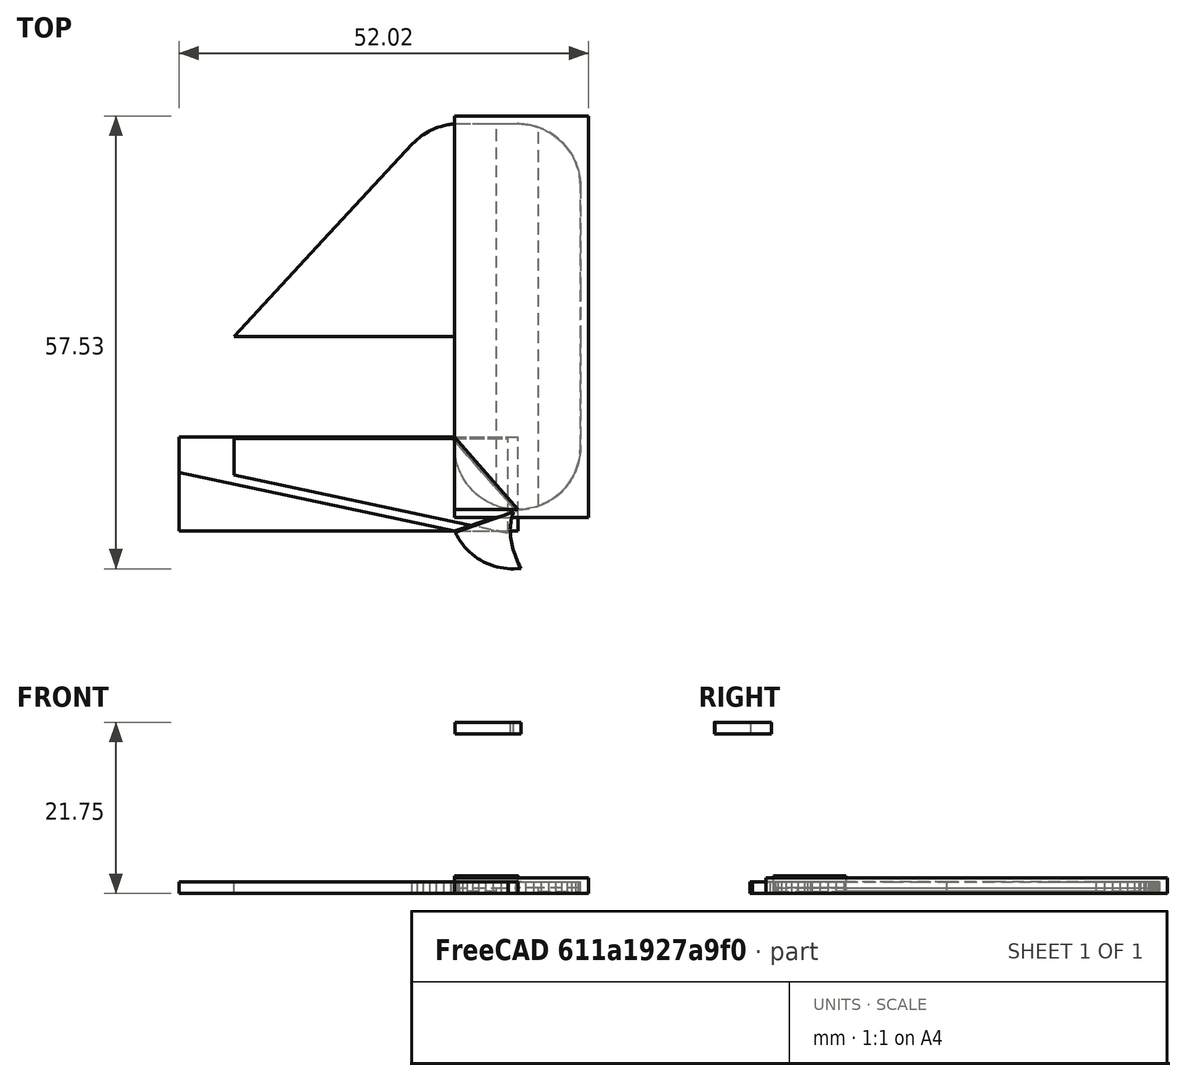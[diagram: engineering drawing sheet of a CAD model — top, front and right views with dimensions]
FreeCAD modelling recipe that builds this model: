
FCSTD DOCUMENT  (FreeCAD 0.18.3R)
Label: Vertical Stabilizer New
License: All rights reserved
LicenseURL: http://en.wikipedia.org/wiki/All_rights_reserved
objects: Part::FeaturePython×24, Part::Feature×8, App::DocumentObjectGroup×6, Part::Extrusion×5, Part::Box×4, Sketcher::SketchObject×4, Mesh::Feature×2, Part::Face×2, Part::Fillet×1
note: 48 computed .brp shape members not serialized (recipe doc carries the construction recipe); baked Part::Feature solids carry a one-line shape summary decoded from their .brp

FEATURE [Mesh::Feature] Vertical_Stabilizer  label="Vertical Stabilizer"
FEATURE [Part::Feature] Vertical_Stabilizer001
  shape: bbox 55.59 x 60.75 x 1.502 mm, 2716 faces, 0 solids (baked)
FEATURE [Part::Feature] Vertical_Stabilizer001_cs
  Placement = pos=(-6.8,0,-0.75) rot=(0,0,1;0rad)
  shape: bbox 44 x 49 x 3e-07 mm, 0 faces, 0 solids (baked)
FEATURE [Mesh::Feature] Fuselage_Full  label="Fuselage Full"
  Placement = pos=(0,0,0) rot=(0,0,1;-1.5708rad)
FEATURE [Part::Face] Face
  FaceMakerClass = Part::FaceMakerBullseye
  Sources = -> [Vertical_Stabilizer001_cs]
FEATURE [Part::Extrusion] Extrude
  Base = -> Face
  Dir = (0,0,1)
  DirMode = 0
  FaceMakerClass = Part::FaceMakerBullseye
  LengthFwd = 1.5
  LengthRev = 0
  Solid = false
  Symmetric = false
FEATURE [Part::Box] Box003  label="Cube003"
  AttacherType = Attacher::AttachEngine3D
  Height = 1.5
  Length = 34.8186
  Placement = pos=(0,-3,0) rot=(0,0,1;0rad)
  Width = 12
FEATURE [Part::Feature] Face004
  Placement = pos=(0,4.3651,0) rot=(0,0,-1;0.208436rad)
  shape: bbox 41.09 x 8.691 x 10 mm, 1 faces, 0 solids (baked)
FEATURE [Part::FeaturePython] Slice003  # WARN: FeaturePython — macro-defined, semantics opaque (R4)
  Base = -> Box003
  Mode = 1
  Tolerance = 0
  Tools = -> [Face004]
FEATURE [Part::FeaturePython] Slice003_child1  label="Slice003.1"  # WARN: FeaturePython — macro-defined, semantics opaque (R4)
  Base = -> Slice003
  FilterType = 1
  Invert = false
  OverrideMaxVal = 0
  WindowFrom = 80
  WindowTo = 100
  items = 1
FEATURE [Part::Feature] Fuselage_Full001
  Placement = pos=(28.0186,13.3054,0) rot=(-1,0,0;1.5708rad)
  shape: bbox 193.7 x 39.83 x 30.14 mm, 4342 faces, 0 solids (baked)
  expr: Placement.Base.y = 13 + 22 - 21.6946
FEATURE [Part::Box] Box  label="Cube"
  AttacherType = Attacher::AttachEngine3D
  Height = 1.5
  Length = 43.0686
  Placement = pos=(-7,-2.6946,0) rot=(0,0,1;0rad)
  Width = 11.9046
FEATURE [Part::Feature] Face005
  Placement = pos=(-7,4.713,0) rot=(0,0,-1;0.208436rad)
  shape: bbox 41.09 x 8.691 x 10 mm, 1 faces, 0 solids (baked)
FEATURE [Sketcher::SketchObject] Sketch
  sketch-geometry (1):
    g0: LineSegment StartX=36.1937 StartY=-0.139812 StartZ=0 EndX=27.8016 EndY=9.45806 EndZ=0
FEATURE [Part::Extrusion] Extrude001
  Base = -> Sketch
  Dir = (0,0,1)
  DirMode = 0
  FaceMakerClass = Part::FaceMakerBullseye
  LengthFwd = 10
  LengthRev = 0
  Placement = pos=(0,0,-1) rot=(0,0,1;0rad)
  Solid = false
  Symmetric = false
FEATURE [Part::FeaturePython] Slice004  # WARN: FeaturePython — macro-defined, semantics opaque (R4)
  Base = -> Extrude
  Mode = 1
  Tolerance = 0
  Tools = -> [Extrude001]
FEATURE [Part::FeaturePython] Slice004_child0  label="Slice004.0"  # WARN: FeaturePython — macro-defined, semantics opaque (R4)
  Base = -> Slice004
  FilterType = 1
  Invert = false
  OverrideMaxVal = 0
  WindowFrom = 80
  WindowTo = 100
  items = 0
FEATURE [Part::FeaturePython] Slice004_child1  label="Slice004.1"  # WARN: FeaturePython — macro-defined, semantics opaque (R4)
  Base = -> Slice004
  FilterType = 1
  Invert = false
  OverrideMaxVal = 0
  WindowFrom = 80
  WindowTo = 100
  items = 1
FEATURE [App::DocumentObjectGroup] GrExplode_Slice004  label="Exploded Slice004"
  Group = -> [Slice004_child0,Slice004_child1]
FEATURE [Sketcher::SketchObject] Sketch001
  sketch-geometry (1):
    g0: LineSegment StartX=37.0114 StartY=-1.03836 StartZ=0 EndX=26.593 EndY=10.8632 EndZ=0
FEATURE [Part::Extrusion] Extrude002
  Base = -> Sketch001
  Dir = (0,0,1)
  DirMode = 0
  FaceMakerClass = Part::FaceMakerBullseye
  LengthFwd = 10
  LengthRev = 0
  Placement = pos=(0,-0.5,0) rot=(0,0,1;0rad)
  Solid = false
  Symmetric = false
FEATURE [Part::FeaturePython] Slice  # WARN: FeaturePython — macro-defined, semantics opaque (R4)
  Base = -> Box
  Mode = 1
  Tolerance = 0
  Tools = -> [Extrude002,Face005]
FEATURE [Part::FeaturePython] Slice_child0  label="Slice.0"  # WARN: FeaturePython — macro-defined, semantics opaque (R4)
  Base = -> Slice
  FilterType = 1
  Invert = false
  OverrideMaxVal = 0
  WindowFrom = 80
  WindowTo = 100
  items = 0
FEATURE [Part::FeaturePython] Slice_child1  label="Slice.1"  # WARN: FeaturePython — macro-defined, semantics opaque (R4)
  Base = -> Slice
  FilterType = 1
  Invert = false
  OverrideMaxVal = 0
  WindowFrom = 80
  WindowTo = 100
  items = 1
FEATURE [Part::FeaturePython] Slice_child2  label="Slice.2"  # WARN: FeaturePython — macro-defined, semantics opaque (R4)
  Base = -> Slice
  FilterType = 1
  Invert = false
  OverrideMaxVal = 0
  WindowFrom = 80
  WindowTo = 100
  items = 2
FEATURE [App::DocumentObjectGroup] GrExplode_Slice  label="Exploded Slice"
  Group = -> [Slice_child0,Slice_child1,Slice_child2]
FEATURE [Sketcher::SketchObject] Sketch002
  sketch-geometry (1):
    g0: LineSegment StartX=27.553 StartY=-2.84984 StartZ=0 EndX=36.7392 EndY=0.230446 EndZ=0
FEATURE [Part::Extrusion] Extrude003
  Base = -> Sketch002
  Dir = (0,0,1)
  DirMode = 0
  FaceMakerClass = Part::FaceMakerBullseye
  LengthFwd = 10
  LengthRev = 0
  Solid = false
  Symmetric = false
FEATURE [Part::FeaturePython] Slice005  # WARN: FeaturePython — macro-defined, semantics opaque (R4)
  Base = -> Slice_child1
  Mode = 1
  Tolerance = 0
  Tools = -> [Extrude003]
FEATURE [Part::FeaturePython] Slice005_child0  label="Slice005.0"  # WARN: FeaturePython — macro-defined, semantics opaque (R4)
  Base = -> Slice005
  FilterType = 1
  Invert = false
  OverrideMaxVal = 0
  WindowFrom = 80
  WindowTo = 100
  items = 0
FEATURE [Part::FeaturePython] Slice005_child1  label="Slice005.1"  # WARN: FeaturePython — macro-defined, semantics opaque (R4)
  Base = -> Slice005
  FilterType = 1
  Invert = false
  OverrideMaxVal = 0
  WindowFrom = 80
  WindowTo = 100
  items = 1
FEATURE [App::DocumentObjectGroup] GrExplode_Slice005  label="Exploded Slice005"
  Group = -> [Slice005_child0,Slice005_child1]
FEATURE [Sketcher::SketchObject] Sketch003
  Placement = pos=(0,0,0) rot=(0.57735,0.57735,0.57735;2.0944rad)
  sketch-geometry (8):
    g0: ArcOfCircle CenterX=4.80291 CenterY=13.5021 CenterZ=0 NormalX=0 NormalY=0 NormalZ=1 AngleXU=0 Radius=8.0992 StartAngle=0.312078 EndAngle=1.57016
    g1: LineSegment StartX=12.5109 StartY=15.9888 StartZ=0 EndX=4.81551 EndY=14.3722 EndZ=0
    g2: Circle [constr] CenterX=4.81551 CenterY=14.3722 CenterZ=0 NormalX=0 NormalY=0 NormalZ=1 AngleXU=0 Radius=0.5
    g3: Circle [constr] CenterX=6.40585 CenterY=17.256 CenterZ=0 NormalX=0 NormalY=0 NormalZ=1 AngleXU=0 Radius=0.5
    g4: Circle [constr] CenterX=4.80807 CenterY=21.6013 CenterZ=0 NormalX=0 NormalY=0 NormalZ=1 AngleXU=0 Radius=0.5
    g5: BSplineCurve PolesCount=3 KnotsCount=2 Degree=2 IsPeriodic=0
    g6: GeomPoint [constr] X=4.81551 Y=14.3722 Z=0
    g7: GeomPoint [constr] X=4.80807 Y=21.6013 Z=0
  constraints (11):
    c: Coincident(g1,g0)
    c: Coincident(g5,g1)
    c: Radius(g2) = 0.5
    c: Equal(g2,g3)
    c: Equal(g2,g4)
    c: Coincident(g5,g0)
    c: InternalAlignment(g2,g5)
    c: InternalAlignment(g3,g5)
    c: InternalAlignment(g4,g5)
    c: InternalAlignment(g6,g5)
    c: InternalAlignment(g7,g5)
FEATURE [Part::Face] Face006
  FaceMakerClass = Part::FaceMakerBullseye
  Placement = pos=(20.25,0,0) rot=(0,0,1;0rad)
  Sources = -> [Sketch003]
FEATURE [Part::Extrusion] Extrude004  label="Tail Skid"
  Base = -> Face006
  Dir = (1,0,0)
  DirMode = 0
  FaceMakerClass = Part::FaceMakerBullseye
  LengthFwd = 1.5
  LengthRev = 0
  Placement = pos=(38.4764,14.5681,0) rot=(0.600348,-0.52836,0.600348;2.16943rad)
  Solid = false
  Symmetric = false
FEATURE [Part::Box] Box005  label="Cube005"
  AttacherType = Attacher::AttachEngine3D
  Height = 0.75
  Length = 16
  Placement = pos=(28.0186,0,1.5) rot=(0,0,1;0rad)
  Width = 49
FEATURE [Part::Fillet] Fillet001
  Base = -> Box005
  Edges = 2 edges r=8: [Edge5,Edge7]
FEATURE [Part::FeaturePython] Slice006  # WARN: FeaturePython — macro-defined, semantics opaque (R4)
  Base = -> Fillet001
  Mode = 1
  Tolerance = 0
  Tools = -> [Extrude001]
FEATURE [Part::FeaturePython] Slice006_child0  label="Slice006.0"  # WARN: FeaturePython — macro-defined, semantics opaque (R4)
  Base = -> Slice006
  FilterType = 1
  Invert = false
  OverrideMaxVal = 0
  Placement = pos=(0,0,-1.5) rot=(0,0,1;0rad)
  WindowFrom = 80
  WindowTo = 100
  items = 0
FEATURE [Part::FeaturePython] Slice006_child1  label="Slice006.1"  # WARN: FeaturePython — macro-defined, semantics opaque (R4)
  Base = -> Slice006
  FilterType = 1
  Invert = false
  OverrideMaxVal = 0
  WindowFrom = 80
  WindowTo = 100
  items = 1
FEATURE [App::DocumentObjectGroup] GrExplode_Slice006  label="Exploded Slice006"
  Group = -> [Slice006_child0,Slice006_child1]
FEATURE [Part::Box] Box006  label="Cube006"
  AttacherType = Attacher::AttachEngine3D
  Height = 2
  Length = 17
  Placement = pos=(28.0176,-1,0) rot=(0,0,1;0rad)
  Width = 51
FEATURE [Part::FeaturePython] Slice007  # WARN: FeaturePython — macro-defined, semantics opaque (R4)
  Base = -> Slice004_child0
  Mode = 1
  Tolerance = 0
  Tools = -> [Box006]
FEATURE [Part::FeaturePython] Slice007_child0  label="VStab Fore"  # WARN: FeaturePython — macro-defined, semantics opaque (R4)
  Base = -> Slice007
  FilterType = 1
  Invert = false
  OverrideMaxVal = 0
  WindowFrom = 80
  WindowTo = 100
  items = 0
FEATURE [Part::FeaturePython] Slice007_child1  label="Slice007.1"  # WARN: FeaturePython — macro-defined, semantics opaque (R4)
  Base = -> Slice007
  FilterType = 1
  Invert = false
  OverrideMaxVal = 0
  WindowFrom = 80
  WindowTo = 100
  items = 1
FEATURE [App::DocumentObjectGroup] GrExplode_Slice007  label="Exploded Slice007"
  Group = -> [Slice007_child0,Slice007_child1]
FEATURE [Part::Feature] Face007
  Placement = pos=(33.3506,-1,0.25) rot=(0,0,1;0rad)
  shape: bbox 2e-07 x 51 x 2 mm, 1 faces, 0 solids (baked)
  expr: Placement.Base.x = 28.0176 + 5.333
FEATURE [Part::Feature] Face008
  Placement = pos=(21.6846,-1,0.25) rot=(0,0,1;0rad)
  shape: bbox 2e-07 x 51 x 2 mm, 1 faces, 0 solids (baked)
  expr: Placement.Base.x = 27.0176 - 5.333
FEATURE [Part::Feature] Face012
  Placement = pos=(28.0176,-1,-1.75) rot=(0,0,1;0rad)
  shape: bbox 17 x 51 x 2e-07 mm, 1 faces, 0 solids (baked)
FEATURE [Part::FeaturePython] Slice008  # WARN: FeaturePython — macro-defined, semantics opaque (R4)
  Base = -> Slice006_child0
  Mode = 1
  Tolerance = 0
  Tools = -> [Face012,Face007,Face008]
FEATURE [Part::FeaturePython] Slice008_child0  label="Slice008.0"  # WARN: FeaturePython — macro-defined, semantics opaque (R4)
  Base = -> Slice008
  FilterType = 1
  Invert = false
  OverrideMaxVal = 0
  WindowFrom = 80
  WindowTo = 100
  items = 0
FEATURE [Part::FeaturePython] Slice008_child1  label="Slice008.1"  # WARN: FeaturePython — macro-defined, semantics opaque (R4)
  Base = -> Slice008
  FilterType = 1
  Invert = false
  OverrideMaxVal = 0
  WindowFrom = 80
  WindowTo = 100
  items = 1
FEATURE [Part::FeaturePython] Slice008_child2  label="Slice008.2"  # WARN: FeaturePython — macro-defined, semantics opaque (R4)
  Base = -> Slice008
  FilterType = 1
  Invert = false
  OverrideMaxVal = 0
  WindowFrom = 80
  WindowTo = 100
  items = 2
FEATURE [Part::FeaturePython] Slice008_child3  label="Fin Flash Blue"  # WARN: FeaturePython — macro-defined, semantics opaque (R4)
  Base = -> Slice008
  FilterType = 1
  Invert = false
  OverrideMaxVal = 0
  WindowFrom = 80
  WindowTo = 100
  items = 3
FEATURE [App::DocumentObjectGroup] GrExplode_Slice008  label="Exploded Slice008"
  Group = -> [Slice008_child0,Slice008_child1,Slice008_child2,Slice008_child3]
FEATURE [Part::FeaturePython] Connect  label="Fin Flash White"  # WARN: FeaturePython — macro-defined, semantics opaque (R4)
  Objects = -> [Slice008_child2,Slice008_child1]
  Tolerance = 0
